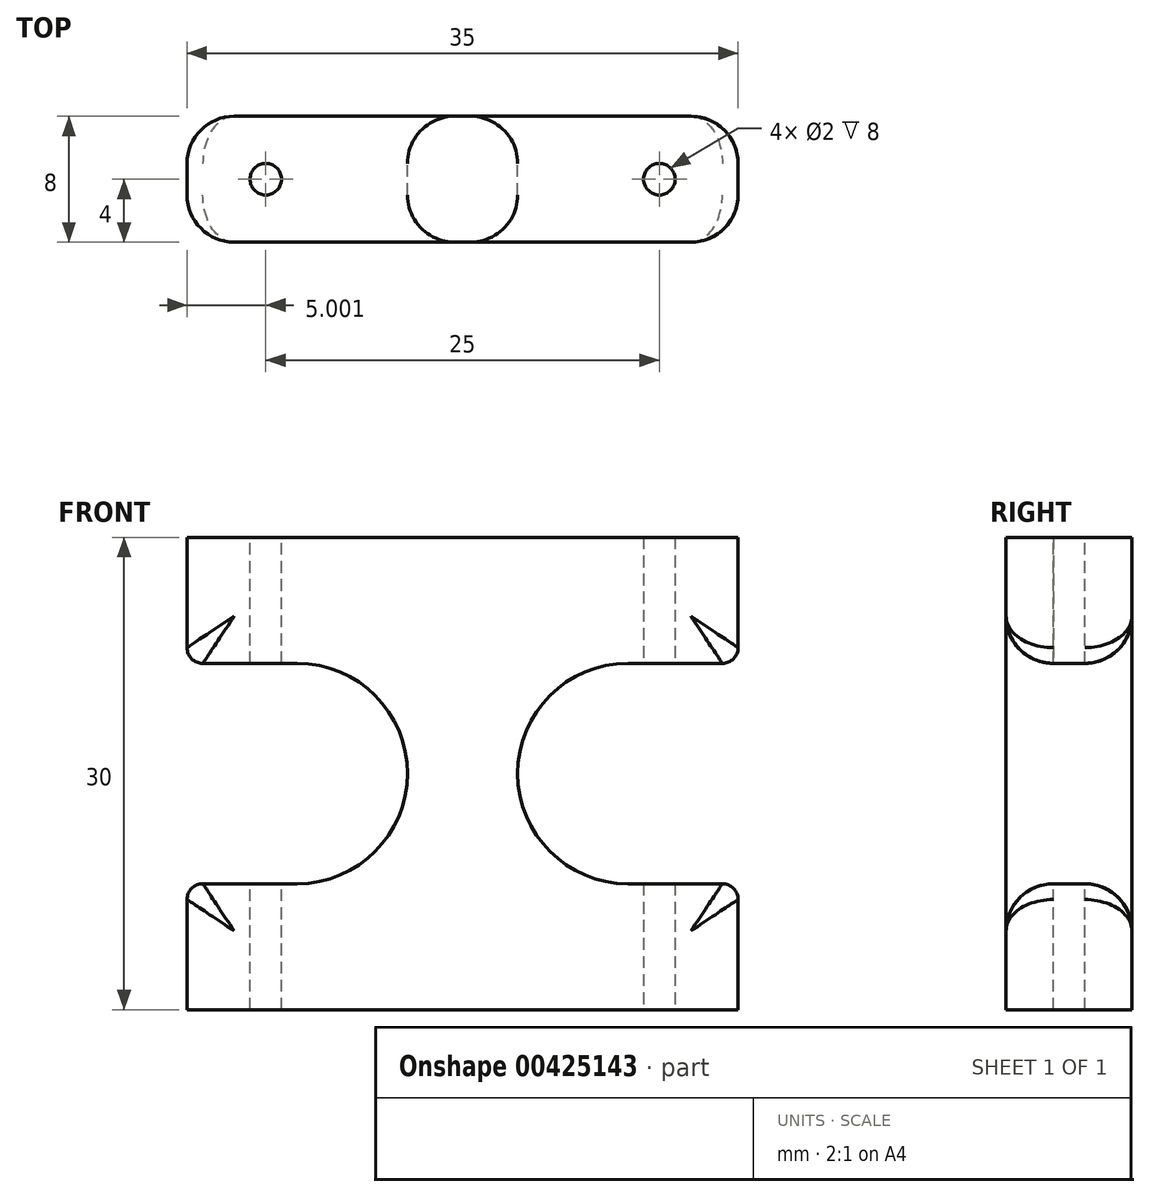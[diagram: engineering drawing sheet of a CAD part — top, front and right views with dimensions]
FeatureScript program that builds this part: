
annotation { "Feature Type Name" : "Feature", "Feature Type Description" : "" }
export const myFeature = defineFeature(function(context is Context, id is Id, definition is map)
    precondition{}
    {
        {
            var Q0;
            Q0=qCreatedBy(makeId("Front.planeOp"),FACE);
            var sketch = newSketch(context, id + "F0", { "sketchPlane" : qUnion([Q0])});
            skLineSegment(sketch, "E0", {"start": v(-31.55, 30.58) * mm, "end": v(-31.55, 38.58) * mm});
            skLineSegment(sketch, "E1", {"start": v(-31.55, 38.58) * mm, "end": v(3.45, 38.58) * mm});
            skLineSegment(sketch, "E2", {"start": v(3.45, 38.58) * mm, "end": v(3.45, 30.58) * mm});
            skLineSegment(sketch, "E3", {"start": v(-31.55, 16.58) * mm, "end": v(-31.55, 8.58) * mm});
            skLineSegment(sketch, "E4", {"start": v(-31.55, 8.58) * mm, "end": v(3.45, 8.58) * mm});
            skLineSegment(sketch, "E5", {"start": v(3.45, 8.58) * mm, "end": v(3.45, 16.58) * mm});
            skLineSegment(sketch, "E6", {"start": v(3.45, 30.58) * mm, "end": v(-3.55, 30.58) * mm});
            skLineSegment(sketch, "E7", {"start": v(3.45, 16.58) * mm, "end": v(-3.55, 16.58) * mm});
            skLineSegment(sketch, "E8", {"start": v(-31.55, 30.58) * mm, "end": v(-24.55, 30.58) * mm});
            skLineSegment(sketch, "E9", {"start": v(-31.55, 16.58) * mm, "end": v(-24.55, 16.58) * mm});
            skArc(sketch, "E10", {"start": v(-24.55, 16.58) * mm, "mid": v(-17.55, 23.58) * mm, "end": v(-24.55, 30.58) * mm});
            skArc(sketch, "E11", {"start": v(-3.55, 30.58) * mm, "mid": v(-10.55, 23.58) * mm, "end": v(-3.55, 16.58) * mm});
            skSolve(sketch);
        }
        {
            var Q0;
            Q0 = qSketchRegion(id + "F0", true);
            extrude(context, id + "F1", {"entities" : qUnion([Q0]), "depth" : 8 * mm});
        }
        {
            var Q0;
            Q0=makeQuery(id+"F1.opExtrude","SWEPT_FACE",FACE,{"disambiguationData":[OSD([sQuery(id+"F0.wireOp",EDGE,"E1")])]});
            var sketch = newSketch(context, id + "F2", { "sketchPlane" : qUnion([Q0])});
            skPoint(sketch, "E12", {"position": v(-26.55, -4) * mm});
            skSolve(sketch);
        }
        {
            var Q0;
            Q0=sQuery(id+"F2.wireOp",VERTEX,"E12");
            var Q1;
            Q1=makeQuery(id+"F1.opExtrude","SWEPT_BODY",BODY,{"disambiguationData":[OSD([sQuery(id+"F0.wireOp",EDGE,"E0"),sQuery(id+"F0.wireOp",EDGE,"E1"),sQuery(id+"F0.wireOp",EDGE,"E2"),sQuery(id+"F0.wireOp",EDGE,"E3"),sQuery(id+"F0.wireOp",EDGE,"E4"),sQuery(id+"F0.wireOp",EDGE,"E5"),sQuery(id+"F0.wireOp",EDGE,"E6"),sQuery(id+"F0.wireOp",EDGE,"E7"),sQuery(id+"F0.wireOp",EDGE,"E8"),sQuery(id+"F0.wireOp",EDGE,"E9"),sQuery(id+"F0.wireOp",EDGE,"E10"),sQuery(id+"F0.wireOp",EDGE,"E11")])]});
            hole(context, id + "F3", {"style" : HoleStyle.SIMPLE, "endStyle" : HoleEndStyle.THROUGH, "holeDiameter" : 2 * mm, "isTappedThrough" : true, "tappedDepth" : 12 * mm, "tapClearance" : 3, "locations" : qUnion([Q0]), "scope" : qUnion([Q1])});
        }
        {
            var Q0;
            Q0=makeQuery(id+"F1.opExtrude","SWEPT_FACE",FACE,{"disambiguationData":[OSD([sQuery(id+"F0.wireOp",EDGE,"E4")])]});
            var sketch = newSketch(context, id + "F4", { "sketchPlane" : qUnion([Q0])});
            skPoint(sketch, "E13", {"position": v(-1.55, 4) * mm});
            skSolve(sketch);
        }
        {
            var Q0;
            Q0=sQuery(id+"F4.wireOp",VERTEX,"E13");
            var Q1;
            Q1=makeQuery(id+"F1.opExtrude","SWEPT_BODY",BODY,{"disambiguationData":[OSD([sQuery(id+"F0.wireOp",EDGE,"E0"),sQuery(id+"F0.wireOp",EDGE,"E1"),sQuery(id+"F0.wireOp",EDGE,"E2"),sQuery(id+"F0.wireOp",EDGE,"E3"),sQuery(id+"F0.wireOp",EDGE,"E4"),sQuery(id+"F0.wireOp",EDGE,"E5"),sQuery(id+"F0.wireOp",EDGE,"E6"),sQuery(id+"F0.wireOp",EDGE,"E7"),sQuery(id+"F0.wireOp",EDGE,"E8"),sQuery(id+"F0.wireOp",EDGE,"E9"),sQuery(id+"F0.wireOp",EDGE,"E10"),sQuery(id+"F0.wireOp",EDGE,"E11")])]});
            hole(context, id + "F5", {"style" : HoleStyle.SIMPLE, "endStyle" : HoleEndStyle.THROUGH, "holeDiameter" : 2 * mm, "isTappedThrough" : true, "tappedDepth" : 12 * mm, "tapClearance" : 3, "locations" : qUnion([Q0]), "scope" : qUnion([Q1])});
        }
        {
            var Q0;
            Q0=makeQuery(id+"F1.opExtrude","CAP_EDGE",EDGE,{"disambiguationData":[OSD([sQuery(id+"F0.wireOp",EDGE,"E0")])],"isStart":false});
            var Q1;
            Q1=makeQuery(id+"F1.opExtrude","CAP_EDGE",EDGE,{"disambiguationData":[OSD([sQuery(id+"F0.wireOp",EDGE,"E3")])],"isStart":false});
            var Q2;
            Q2=makeQuery(id+"F1.opExtrude","CAP_EDGE",EDGE,{"disambiguationData":[OSD([sQuery(id+"F0.wireOp",EDGE,"E10")])],"isStart":false});
            var Q3;
            Q3=makeQuery(id+"F1.opExtrude","CAP_EDGE",EDGE,{"disambiguationData":[OSD([sQuery(id+"F0.wireOp",EDGE,"E3")])],"isStart":true});
            var Q4;
            Q4=makeQuery(id+"F1.opExtrude","CAP_EDGE",EDGE,{"disambiguationData":[OSD([sQuery(id+"F0.wireOp",EDGE,"E0")])],"isStart":true});
            var Q5;
            Q5=makeQuery(id+"F1.opExtrude","SWEPT_FACE",FACE,{"disambiguationData":[OSD([sQuery(id+"F0.wireOp",EDGE,"E10")])]});
            var Q6;
            Q6=makeQuery(id+"F1.opExtrude","CAP_EDGE",EDGE,{"disambiguationData":[OSD([sQuery(id+"F0.wireOp",EDGE,"E11")])],"isStart":true});
            var Q7;
            Q7=makeQuery(id+"F1.opExtrude","CAP_EDGE",EDGE,{"disambiguationData":[OSD([sQuery(id+"F0.wireOp",EDGE,"E5")])],"isStart":true});
            var Q8;
            Q8=makeQuery(id+"F1.opExtrude","CAP_EDGE",EDGE,{"disambiguationData":[OSD([sQuery(id+"F0.wireOp",EDGE,"E2")])],"isStart":true});
            var Q9;
            Q9=makeQuery(id+"F1.opExtrude","CAP_EDGE",EDGE,{"disambiguationData":[OSD([sQuery(id+"F0.wireOp",EDGE,"E5")])],"isStart":false});
            var Q10;
            Q10=makeQuery(id+"F1.opExtrude","CAP_EDGE",EDGE,{"disambiguationData":[OSD([sQuery(id+"F0.wireOp",EDGE,"E2")])],"isStart":false});
            var Q11;
            Q11=makeQuery(id+"F1.opExtrude","SWEPT_FACE",FACE,{"disambiguationData":[OSD([sQuery(id+"F0.wireOp",EDGE,"E11")])]});
            fillet(context, id + "F6", {"entities" : qUnion([Q0, Q1, Q2, Q3, Q4, Q5, Q6, Q7, Q8, Q9, Q10, Q11]), "radius" : 3 * mm, "tangentPropagation" : true, "allowEdgeOverflow" : false});
        }
        {
            var Q0;
            Q0=makeQuery(id+"F1.opExtrude","SWEPT_EDGE",EDGE,{"disambiguationData":[OSD([sQuery(id+"F0.wireOp",EDGE,"E2"),sQuery(id+"F0.wireOp",EDGE,"E6")])]});
            var Q1;
            Q1=makeQuery(id+"F1.opExtrude","SWEPT_EDGE",EDGE,{"disambiguationData":[OSD([sQuery(id+"F0.wireOp",EDGE,"E5"),sQuery(id+"F0.wireOp",EDGE,"E7")])]});
            var Q2;
            Q2=makeQuery(id+"F1.opExtrude","SWEPT_EDGE",EDGE,{"disambiguationData":[OSD([sQuery(id+"F0.wireOp",EDGE,"E3"),sQuery(id+"F0.wireOp",EDGE,"E9")])]});
            var Q3;
            Q3=makeQuery(id+"F1.opExtrude","SWEPT_EDGE",EDGE,{"disambiguationData":[OSD([sQuery(id+"F0.wireOp",EDGE,"E0"),sQuery(id+"F0.wireOp",EDGE,"E8")])]});
            fillet(context, id + "F7", {"entities" : qUnion([Q0, Q1, Q2, Q3]), "radius" : 1 * mm, "tangentPropagation" : true, "allowEdgeOverflow" : false});
        }
    });
